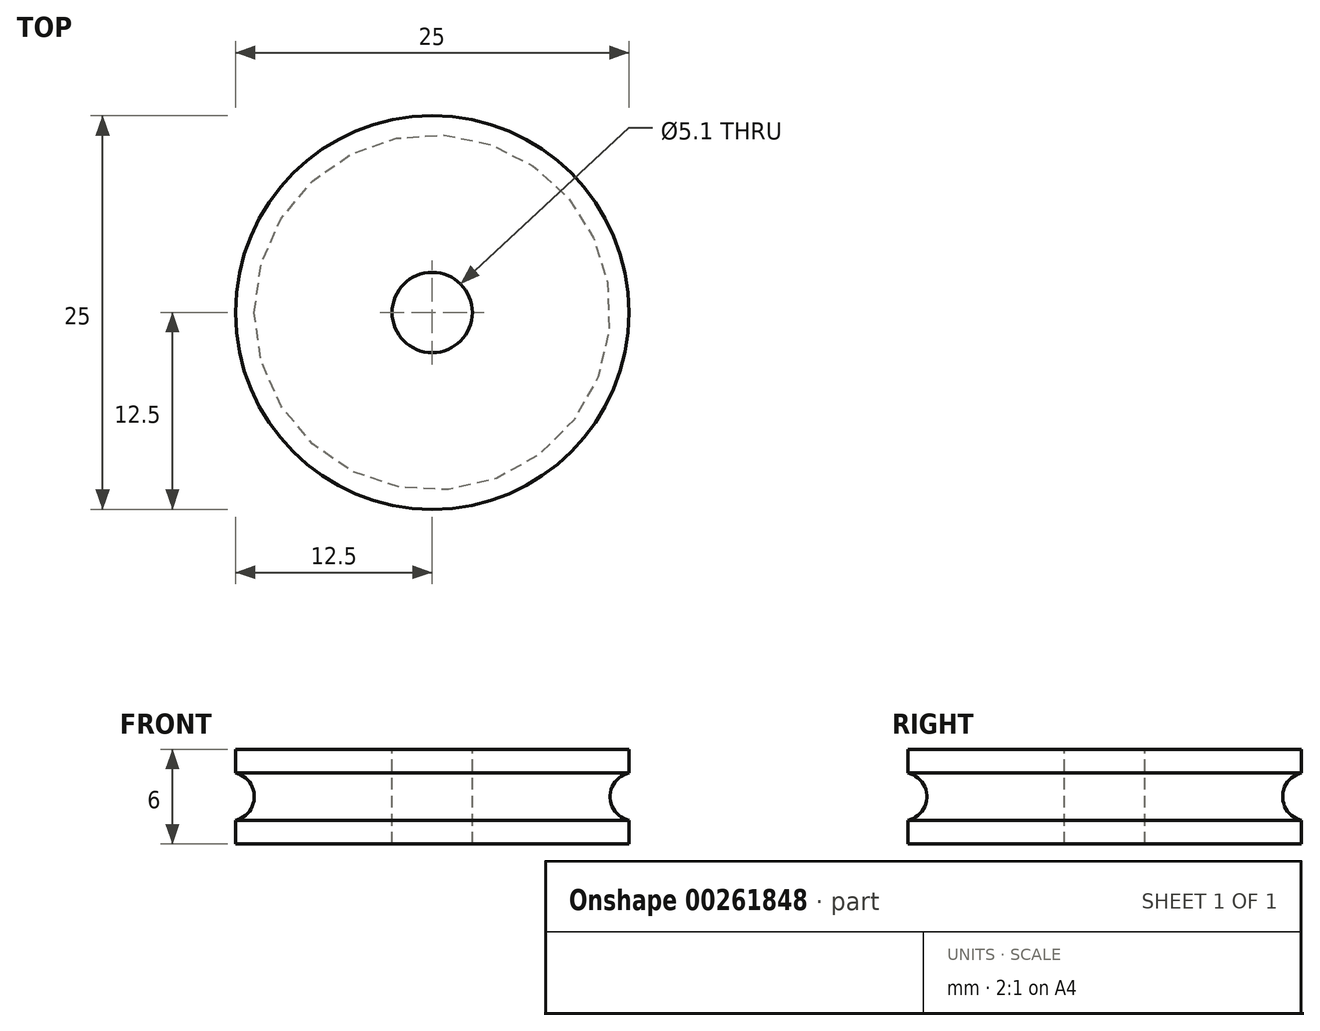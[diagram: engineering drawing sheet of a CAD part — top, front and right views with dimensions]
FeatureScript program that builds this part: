
annotation { "Feature Type Name" : "Feature", "Feature Type Description" : "" }
export const myFeature = defineFeature(function(context is Context, id is Id, definition is map)
    precondition{}
    {
        {
            var Q0;
            Q0=qCreatedBy(makeId("Front.planeOp"),FACE);
            var sketch = newSketch(context, id + "F0", { "sketchPlane" : qUnion([Q0])});
            skLineSegment(sketch, "E0", {"start": v(0, 0) * mm, "end": v(-12.5, 0) * mm});
            skLineSegment(sketch, "E1", {"start": v(-12.5, 0) * mm, "end": v(-12.5, 1.5) * mm});
            skLineSegment(sketch, "E2", {"start": v(0, 3) * mm, "end": v(-18.74, 3) * mm, "construction": true});
            skLineSegment(sketch, "E3.MirrorCS", {"start": v(-12.5, 6) * mm, "end": v(-12.5, 4.5) * mm});
            skLineSegment(sketch, "E4.MirrorCS", {"start": v(0, 6) * mm, "end": v(-12.5, 6) * mm});
            skArc(sketch, "E5", {"start": v(-12.5, 1.5) * mm, "mid": v(-11.3, 3) * mm, "end": v(-12.5, 4.5) * mm});
            skLineSegment(sketch, "E6", {"start": v(0, 0) * mm, "end": v(0, 6) * mm});
            skLineSegment(sketch, "E7", {"start": v(-11.3, 6) * mm, "end": v(-11.3, 0) * mm, "construction": true});
            skSolve(sketch);
        }
        {
            var Q0;
            Q0=qSketchRegion(id+"F0",true);
            var Q1;
            Q1=sQuery(id+"F0.wireOp",EDGE,"E6");
            revolve(context, id + "F1", {"entities" : qUnion([Q0]), "axis" : qUnion([Q1]), "revolveType" : RevolveType.FULL});
        }
        {
            var Q0;
            Q0=makeQuery(id+"F1.opRevolve","SWEPT_FACE",FACE,{"disambiguationData":[OSD([sQuery(id+"F0.wireOp",EDGE,"E4.MirrorCS")])]});
            var sketch = newSketch(context, id + "F2", { "sketchPlane" : qUnion([Q0])});
            skPoint(sketch, "E8", {"position": v(0, 0) * mm});
            skSolve(sketch);
        }
        {
            var Q0;
            Q0=sQuery(id+"F2.wireOp",VERTEX,"E8");
            var Q1;
            Q1=makeQuery(id+"F1.opRevolve","SWEPT_BODY",BODY,{"disambiguationData":[OSD([sQuery(id+"F0.wireOp",EDGE,"E0"),sQuery(id+"F0.wireOp",EDGE,"E1"),sQuery(id+"F0.wireOp",EDGE,"E3.MirrorCS"),sQuery(id+"F0.wireOp",EDGE,"E4.MirrorCS"),sQuery(id+"F0.wireOp",EDGE,"E5"),sQuery(id+"F0.wireOp",EDGE,"E6")])]});
            hole(context, id + "F3", {"style" : HoleStyle.SIMPLE, "endStyle" : HoleEndStyle.THROUGH, "holeDiameter" : 5.1 * mm, "tappedDepth" : 12 * mm, "tapClearance" : 3, "locations" : qUnion([Q0]), "scope" : qUnion([Q1])});
        }
    });
